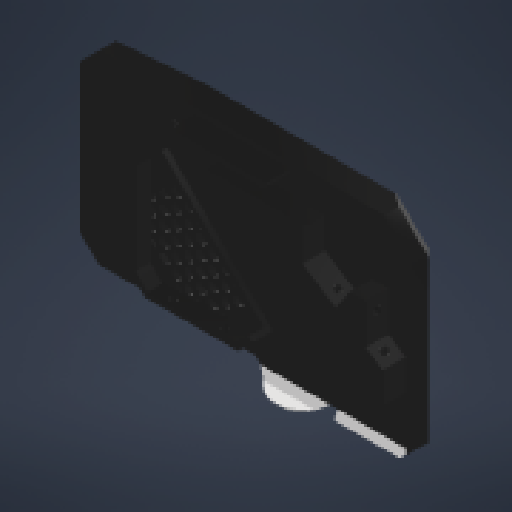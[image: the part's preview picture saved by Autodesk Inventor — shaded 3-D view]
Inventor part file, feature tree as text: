
AUTODESK INVENTOR PART (.ipt)
format: ipt  version: 2024 (Build 280153000, 153)  size: 1,572,864 bytes
history: native  units: in
note: dims shown in document units (in); Inventor stores cm internally (conversion verified against a paired STEP export)
features: reference x17, sketch x15, extrude x15, chamfer x13, projected_geometry x11, plane x6, other x3, fillet x1, mirror x1
ambient origin geometry x8: Origin, YZ Plane, XZ Plane, XY Plane, X Axis, Y Axis, Z Axis, Center Point
bodies: Solid1 (feature_tree)
feature tree (82):
  sketch  "Sketch1"  dims[d0=0.0157in d1=0.1181in]
  plane  "Work Plane1"
  extrude  "Extrusion1"  Depth=0.1181in
  sketch  "Sketch2"  dims[d2=1.0in d3=0.0in d4=0.7874in d6=0.2953in d7=2.3622in d9=0.2953in]
  plane  "Work Plane2"
  extrude  "Extrusion2"  Depth=0.7874in
  extrude  "Extrusion3"  Depth=3.1496in
  extrude  "Extrusion4"  Depth=0.1181in
  extrude  "Extrusion5"  Depth=0.1181in
  extrude  "Extrusion6"  Depth=0.1181in TaperAngle=0.0deg
  chamfer  "Chamfer1"  Distance=0.0394in
  sketch  "Sketch7"  dims[d30=0.25in]
  plane  "Work Plane3"
  extrude  "Extrusion7"  Depth=0.1181in TaperAngle=0.0deg
  extrude  "Extrusion8"  Depth=0.125in TaperAngle=45.0deg
  chamfer  "Chamfer3"  Distance=0.4724in
  chamfer  "Chamfer5"  Distance=1.0in
  chamfer  "Chamfer7"  Distance=0.2756in
  extrude  "Extrusion10"  Depth=0.1181in
  fillet  "Fillet2"  Radius=0.3912in
  chamfer  "Chamfer8"  Distance=0.8843in Angle=15.0deg
  chamfer  "Chamfer9"  Distance=0.0787in Angle=15.0deg
  chamfer  "Chamfer10"  Distance=0.1181in
  chamfer  "Chamfer11"  Distance=0.1181in
  chamfer  "Chamfer12"  Distance=0.42in Angle=15.0deg
  chamfer  "Chamfer13"  Distance=0.545in Angle=15.0deg
  extrude  "Extrusion11"  Depth=0.1181in TaperAngle=15.0deg
  extrude  "Extrusion12"  Depth=0.1181in
  chamfer  "Chamfer14"  Distance=0.0787in
  extrude  "Extrusion13"  Depth=0.1181in
  plane  "Work Plane4"
  mirror  "Mirror1"
  extrude  "Extrusion14"  Depth=0.1181in TaperAngle=0.0deg
  chamfer  "Chamfer15"  Distance=0.1654in
  chamfer  "Chamfer16"  Distance=0.2756in
  sketch  "Sketch15"  dims[d46=0.0118in]
  plane  "Work Plane5"
  extrude  "Extrusion15"  Depth=0.1181in
  sketch  "Sketch16"  dims[d48=0.55in d49=0.4724in d50=0.0in d51=1.0in d52=0.0in d53=0.2756in d54=0.1575in d61=0.3912in d62=0.125in d63=15.0deg d67=0.8843in d68=0.125in d69=15.0deg d73=0.0787in d74=0.125in d75=15.0deg d76=0.1181in d77=0.0in d78=0.1181in d79=0.42in d80=0.125in d81=15.0deg d82=0.545in d83=0.125in d84=15.0deg d85=0.0787in d86=0.125in d87=15.0deg d88=2.1412in d89=0.125in d90=0.0344in d91=0.0787in d92=0.125in d93=0.0344in d94=0.2756in d95=0.125in d96=0.0344in d97=1.0in d98=0.0in d99=0.1654in d100=0.2756in d101=0.0in d102=0.0787in d103=0.125in d104=0.0344in d105=0.0787in d106=45.0deg d107=1.0in d108=0.0in d109=0.1181in d110=2.8125in d111=0.0in d112=0.1969in d113=0.125in d114=45.0deg d115=0.0787in d116=0.125in d117=45.0deg d118=2.8125in d119=0.0in d120=0.0118in d121=0.0118in d122=1.0in d123=0.0in]
  plane  "Work Plane6"
  extrude  "Extrusion16"  Depth=0.1181in
  reference  "Reference1"
  projected_geometry  "Projected Loop1"
  sketch  "Sketch3"  dims[d12=0.1952in d13=3.1496in d15=0.2953in d16=0.7874in d18=0.2953in]
  reference  "Reference2"
  reference  "Reference3"
  sketch  "Sketch4"  dims[d22=1.0in d23=0.0in d24=0.1181in]
  reference  "Reference4"
  reference  "Reference5"
  reference  "Reference6"
  reference  "Reference7"
  reference  "Reference8"
  reference  "Reference9"
  reference  "Reference10"
  sketch  "Sketch5"  dims[d25=0.1181in d26=0.1181in]
  projected_geometry  "Projected Loop2"
  sketch  "Sketch6"  dims[d27=0.1181in d28=1.0in d29=0.0in]
  projected_geometry  "Projected Loop3"
  projected_geometry  "Projected Loop4"
  reference  "Reference11"
  reference  "Reference12"
  reference  "Reference13"
  reference  "Reference14"
  reference  "Reference15"
  projected_geometry  "Projected Loop5"
  sketch  "Sketch8"  dims[d32=0.3937in]
  reference  "Reference16"
  reference  "Reference17"
  sketch  "Sketch10"  dims[d33=0.1181in]
  projected_geometry  "Projected Loop6"
  sketch  "Sketch11"  dims[d34=2.1654in]
  projected_geometry  "Projected Loop7"
  sketch  "Sketch12"  dims[d35=0.0984in d36=0.0394in d37=0.0in]
  projected_geometry  "Projected Loop8"
  sketch  "Sketch13"  dims[d38=0.1181in d39=0.0787in d40=0.0in]
  projected_geometry  "Projected Loop9"
  sketch  "Sketch14"  dims[d41=0.4724in d42=0.0in d43=0.125in d44=0.125in d45=45.0deg]
  projected_geometry  "Projected Loop10"
  projected_geometry  "Projected Loop11"
  other  "<userpath>\Desktop\SeniorDesign\Head_V3\Head_V3_Assembly.iam"
  other  "Head_V3_Assembly.iam"
  other  "Head_base_mount:1"
